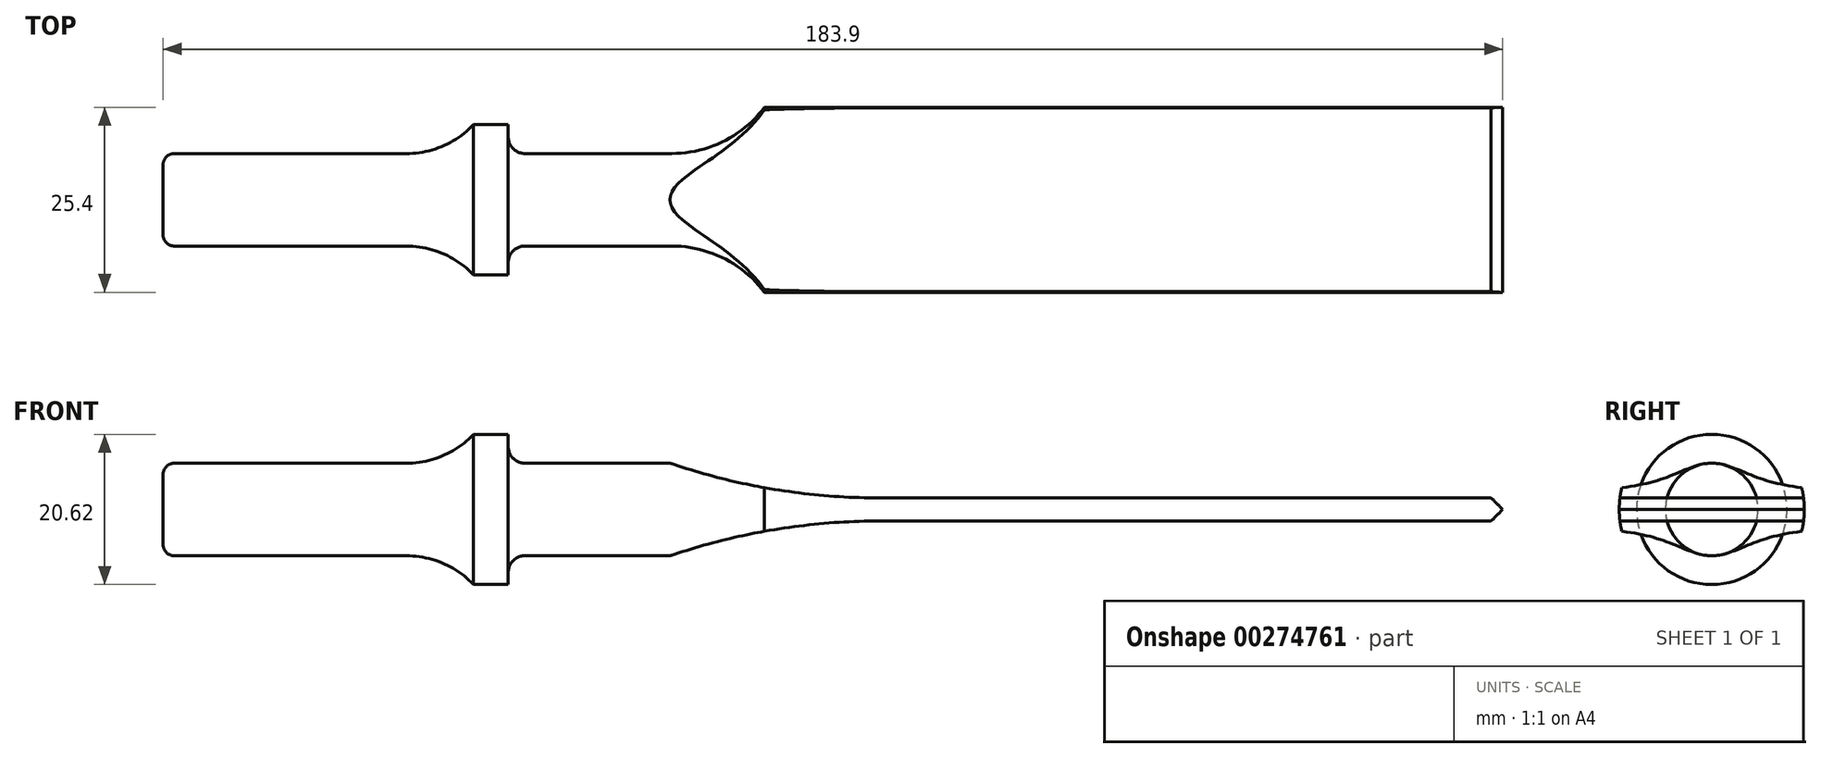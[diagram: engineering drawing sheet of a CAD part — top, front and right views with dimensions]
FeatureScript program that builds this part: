
annotation { "Feature Type Name" : "Feature", "Feature Type Description" : "" }
export const myFeature = defineFeature(function(context is Context, id is Id, definition is map)
    precondition{}
    {
        {
            var Q0;
            Q0=qCreatedBy(makeId("Front.planeOp"),FACE);
            var sketch = newSketch(context, id + "F0", { "sketchPlane" : qUnion([Q0])});
            skLineSegment(sketch, "E0", {"start": v(0, 0) * mm, "end": v(184.15, 0) * mm});
            skLineSegment(sketch, "E1", {"start": v(0, 0) * mm, "end": v(0, 4.83) * mm});
            skLineSegment(sketch, "E2", {"start": v(1.52, 6.35) * mm, "end": v(33.4, 6.35) * mm});
            skLineSegment(sketch, "E3", {"start": v(42.62, 10.31) * mm, "end": v(47.37, 10.31) * mm});
            skLineSegment(sketch, "E4", {"start": v(47.37, 10.31) * mm, "end": v(47.37, 8.64) * mm});
            skLineSegment(sketch, "E5", {"start": v(184.15, 0) * mm, "end": v(184.15, 12.7) * mm});
            skLineSegment(sketch, "E6.0", {"start": v(95.25, 0) * mm, "end": v(95.25, 12.7) * mm, "construction": true});
            skLineSegment(sketch, "E7.0", {"start": v(82.55, 0) * mm, "end": v(82.55, 12.7) * mm, "construction": true});
            skLineSegment(sketch, "E8", {"start": v(184.15, 12.7) * mm, "end": v(82.55, 12.7) * mm});
            skLineSegment(sketch, "E9.trimOffspring", {"start": v(49.66, 6.35) * mm, "end": v(82.55, 6.35) * mm});
            skArc(sketch, "E10", {"start": v(69.85, 6.35) * mm, "mid": v(76.95, 8.03) * mm, "end": v(82.55, 12.7) * mm});
            skArc(sketch, "E11", {"start": v(33.4, 6.35) * mm, "mid": v(38.42, 7.38) * mm, "end": v(42.62, 10.31) * mm});
            skPoint(sketch, "E12.visualSharp", {"position": v(0, 6.35) * mm});
            skArc(sketch, "E12.filletArc", {"start": v(1.52, 6.35) * mm, "mid": v(0.45, 5.9) * mm, "end": v(0, 4.83) * mm});
            skPoint(sketch, "E13.visualSharp", {"position": v(47.37, 6.35) * mm});
            skArc(sketch, "E13.filletArc", {"start": v(47.37, 8.64) * mm, "mid": v(48.04, 7.02) * mm, "end": v(49.66, 6.35) * mm});
            skSolve(sketch);
        }
        {
            var Q0;
            Q0=makeQuery(id+"F0.imprint","IMPRINT",FACE,{"disambiguationData":[TD([[makeQuery(id+"F0.imprint","IMPRINT",EDGE,{"derivedFrom":sQuery(id+"F0.wireOp",EDGE,"E0")}),1.0]])]});
            var Q1;
            Q1=sQuery(id+"F0.wireOp",EDGE,"E0");
            revolve(context, id + "F1", {"entities" : qUnion([Q0]), "axis" : qUnion([Q1]), "revolveType" : RevolveType.FULL});
        }
        {
            var Q0;
            Q0=qCreatedBy(makeId("Front.planeOp"),FACE);
            var sketch = newSketch(context, id + "F2", { "sketchPlane" : qUnion([Q0])});
            skPoint(sketch, "E14.start.orphan", {"position": v(183.9, 32.55) * mm});
            skLineSegment(sketch, "E15.0", {"start": v(69.6, 0) * mm, "end": v(69.6, 6.35) * mm});
            skLineSegment(sketch, "E16.0", {"start": v(0, 6.35) * mm, "end": v(54.08, 6.35) * mm});
            skPoint(sketch, "E17", {"position": v(69.6, 6.35) * mm});
            skLineSegment(sketch, "E18.1", {"start": v(54.08, 1.59) * mm, "end": v(54.08, 0) * mm});
            skPoint(sketch, "E19.orphan", {"position": v(0, 0) * mm});
            skLineSegment(sketch, "E20", {"start": v(183.9, 0) * mm, "end": v(182.31, 1.59) * mm});
            skArc(sketch, "E21", {"start": v(69.6, 6.35) * mm, "mid": v(83.76, 2.79) * mm, "end": v(98.3, 1.59) * mm});
            skLineSegment(sketch, "E22.trimOffspring", {"start": v(183.9, 6.35) * mm, "end": v(183.9, 32.55) * mm});
            skLineSegment(sketch, "E23", {"start": v(69.6, 6.35) * mm, "end": v(82.52, 56.94) * mm});
            skLineSegment(sketch, "E24", {"start": v(82.52, 56.94) * mm, "end": v(124.92, 45) * mm});
            skLineSegment(sketch, "E25", {"start": v(124.92, 45) * mm, "end": v(189.3, 23.9) * mm});
            skLineSegment(sketch, "E26", {"start": v(189.3, 23.9) * mm, "end": v(189.3, 0) * mm});
            skLineSegment(sketch, "E27", {"start": v(189.3, 0) * mm, "end": v(183.9, 0) * mm});
            skLineSegment(sketch, "E28", {"start": v(98.3, 1.59) * mm, "end": v(182.31, 1.59) * mm});
            skLineSegment(sketch, "E29.MirrorCS", {"start": v(69.6, -6.35) * mm, "end": v(82.52, -56.94) * mm});
            skArc(sketch, "E30.MirrorCS", {"start": v(69.6, -6.35) * mm, "mid": v(83.76, -2.79) * mm, "end": v(98.3, -1.59) * mm});
            skLineSegment(sketch, "E31.MirrorCS", {"start": v(82.52, -56.94) * mm, "end": v(124.92, -45) * mm});
            skLineSegment(sketch, "E32.MirrorCS", {"start": v(124.92, -45) * mm, "end": v(189.3, -23.9) * mm});
            skLineSegment(sketch, "E33.MirrorCS", {"start": v(189.3, -23.9) * mm, "end": v(189.3, 0) * mm});
            skLineSegment(sketch, "E34.MirrorCS", {"start": v(98.3, -1.59) * mm, "end": v(182.31, -1.59) * mm});
            skLineSegment(sketch, "E35.MirrorCS", {"start": v(183.9, 0) * mm, "end": v(182.31, -1.59) * mm});
            skPoint(sketch, "E36.trimOffspring.start.orphan", {"position": v(69.6, 1.59) * mm});
            skPoint(sketch, "E37.MirrorCS.end.orphan", {"position": v(98.3, -1.59) * mm});
            skPoint(sketch, "E37.MirrorCS.start.orphan", {"position": v(69.6, -1.59) * mm});
            skSolve(sketch);
        }
        {
            var Q0;
            Q0=makeQuery(id+"F2.imprint","IMPRINT",FACE,{"disambiguationData":[TD([[makeQuery(id+"F2.imprint","IMPRINT",EDGE,{"derivedFrom":sQuery(id+"F2.wireOp",EDGE,"E27")}),1.0]])]});
            var Q1;
            Q1=makeQuery(id+"F2.imprint","IMPRINT",FACE,{"disambiguationData":[TD([[makeQuery(id+"F2.imprint","IMPRINT",EDGE,{"derivedFrom":sQuery(id+"F2.wireOp",EDGE,"E20")}),-1.0]])]});
            extrude(context, id + "F3", {"entities" : qUnion([Q0, Q1]), "operationType" : NewBodyOperationType.REMOVE, "oppositeDirection" : true, "depth" : 25.4 * mm});
        }
        {
            var Q0;
            Q0 = qSketchRegion(id + "F2", true);
            extrude(context, id + "F4", {"entities" : qUnion([Q0]), "operationType" : NewBodyOperationType.REMOVE, "depth" : 25.4 * mm});
        }
    });
